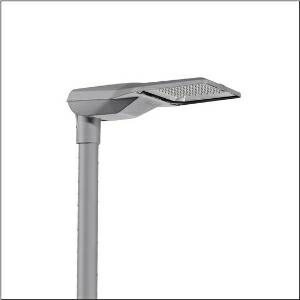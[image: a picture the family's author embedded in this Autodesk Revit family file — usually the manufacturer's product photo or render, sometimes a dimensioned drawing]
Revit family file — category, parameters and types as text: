
# Revit family: streetlight_sl_21_iq_midi___st0_8a_5xe3c61g08nb_b7e9
name_source: partatom
category: Lighting Fixtures
units: mm (PartAtom-declared; Revit-internal decimal feet)

## family parameters
Cut with Voids When Loaded = No
Host = Face
Light Source = No
Part Type = Normal
Room Calculation Point = No
Round Connector Dimension = Use Diameter
Shared = No

## types (1)
- --- (1 x LED, 20820 lm, 155.5 W, 2700K)
    Apparent Load = 155 VA
    CIE Flux Codes = 41 75 97 100 100
    Color Rendering = 70
    Color Temperature = 2700K
    Default Elevation = 1800 mm
    Description = Streetlight SL 21 iQ midi, mast luminaire, primary light control with lens, of PMMA, primary optical cover: cover, of toughened safety glass, transparent, light distribution: ST0.8a, light emission: direct distribution, primary light characteristic: asymmetric, installation type: post-top, side-entry, LED, High Power LED, rated luminous flux: 20.820lm, luminous efficacy: 134lm/W, light colour: 727, colour temperature: 2700K, control gear: iQ Street-Remote, control: Street-Remote, Auto-Match, Temp-Guard, Lumen-Switch, Night-Set, Smart-Wire, Light-Fading, Desk-Remote (wireless, voltage-free reading and setting of iQ features in the workshop via application-optimized NFC function/RFID function), optimised constant luminous flux control (CLO 2.0), pre-setting: linear dimming characteristic, mains connection: 230..240V, AC, 50/60Hz, start of lifetime: 156W, end of service life: 162W, reduction: 69W, luminaire housing, of diecast aluminium, powder-coated, Siteco® metallic grey (DB 702S), corrosivity category C5 mid according to DIN EN ISO 12944, please order mast flange separately, inclination adjustable: 0°, 5°, 10°, 15°, sealing non-destructively replaceable, multi-level sealing system, length: 644mm, width: 335mm, height: 110mm, mast flange for spigot size: 42mm (side-entry): 5XC10008XM4, 60/48mm (side-entry/post-top): 5XC10108XM2, 76/60mm (side-entry/post-top): 5XC10108XM1, mounting height: 4..8m, protection rating (complete): IP66, insulation class (complete): insulation class II (safety insulation), certification: CE, ENEC, ENEC+, VDE, impact resistance: IK10, permissible operating ambient temperature for outdoor applications: -40..+50°C, standard-compliant lighting for roads and squares, packaging unit: 1 piece

Light Distribution: ST0.8a
    Height = 111 mm
    Lamp = 1 x LED
    Lamp Light Flux = 20820 lm
    Lamp Power = 155.5 W
    Lamp count = 1
    Length = 644 mm
    Luminous efficacy = 134 lm/W
    Manufacturer = Siteco
    ModVariant = No
    Model = 5XE3C61G08NB
    Number of Poles = 1
    OnlyDefault = Yes
    Power Factor = 1
    Product Name = Streetlight SL 21 iQ midi | ST0.8a
    Product group = mast luminaire | pylon top
    ProductGroupID = 6100
    Protection Class = Protection class II
    Protection Degree = IP 66
    RLX_Detail_Level = 1
    RLX_Emergency_Light_Flux = 0 lm
    RLX_Emergency_Type = 0
    RLX_Emergency_Type_DB = No
    RlxData = <blob elided: 27229 chars, md5=535a6e78>
    Socket = socket
    Standby Power = 0 W
    System Light Flux = 20820 lm
    System Power = 155 W
    Type Comments = factory setting: luminous flux: 100 % | dim-lin: 254 | 823 mA
    Type Image = l_1004298.jpg
    URL = http://relux.com
    VarID = @adj_168796
    Voltage = 0 V
    Weight = 0.00 kg
    Width = 336 mm

## geometry (parser evidence)
native form markers: Blend x4, Sweep x10
no freeform markers — native parametric forms only
